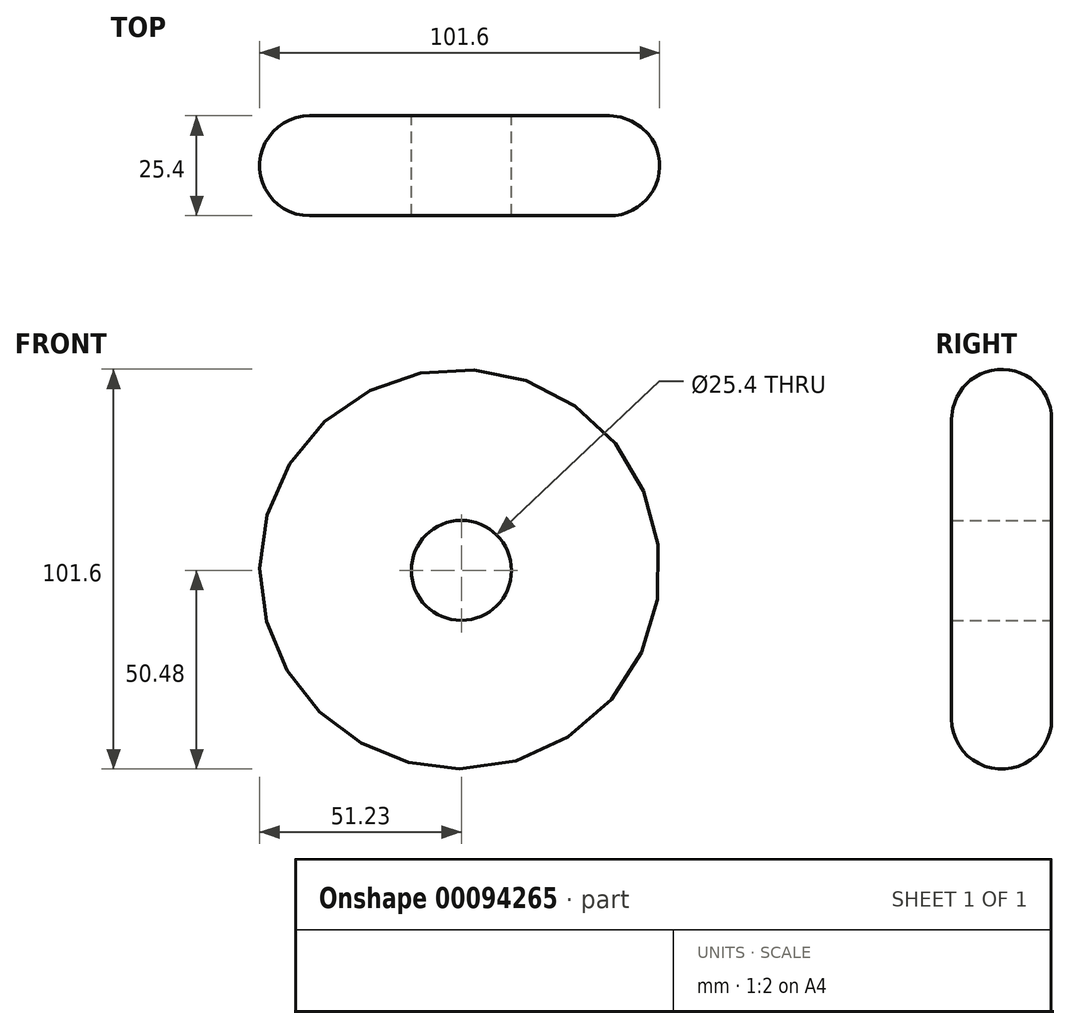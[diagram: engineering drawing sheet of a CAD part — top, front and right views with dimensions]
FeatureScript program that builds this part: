
annotation { "Feature Type Name" : "Feature", "Feature Type Description" : "" }
export const myFeature = defineFeature(function(context is Context, id is Id, definition is map)
    precondition{}
    {
        {
            var Q0;
            Q0=qCreatedBy(makeId("Front.planeOp"),FACE);
            var sketch = newSketch(context, id + "F0", { "sketchPlane" : qUnion([Q0])});
            skCircle(sketch, "E0", {"center": v(0, 0) * mm, "radius": 25.4 * mm});
            skCircle(sketch, "E1", {"center": v(0, 0) * mm, "radius": 12.7 * mm});
            skCircle(sketch, "E2", {"center": v(-0.43, 0.32) * mm, "radius": 50.8 * mm});
            skSolve(sketch);
        }
        {
            var Q0;
            Q0 = qSketchRegion(id + "F0", true);
            var Q1;
            Q1=makeQuery(id+"F0.imprint","IMPRINT",FACE,{"disambiguationData":[TD([[makeQuery(id+"F0.imprint","IMPRINT",EDGE,{"derivedFrom":sQuery(id+"F0.wireOp",EDGE,"E0")}),1.0]])]});
            extrude(context, id + "F1", {"entities" : qUnion([Q0, Q1]), "endBound" : BoundingType.SYMMETRIC, "depth" : 25.4 * mm});
        }
        {
            var Q0;
            Q0=makeQuery(id+"F1.opExtrude","CAP_EDGE",EDGE,{"disambiguationData":[OSD([sQuery(id+"F0.wireOp",EDGE,"E2")])],"isStart":true});
            var Q1;
            Q1=makeQuery(id+"F1.opExtrude","CAP_EDGE",EDGE,{"disambiguationData":[OSD([sQuery(id+"F0.wireOp",EDGE,"E2")])],"isStart":false});
            fillet(context, id + "F2", {"entities" : qUnion([Q0, Q1]), "radius" : 12.7 * mm, "tangentPropagation" : true, "allowEdgeOverflow" : false});
        }
    });
